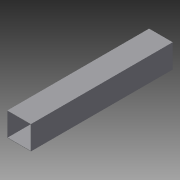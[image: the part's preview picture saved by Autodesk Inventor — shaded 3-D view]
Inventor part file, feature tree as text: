
AUTODESK INVENTOR PART (.ipt)
format: ipt  version: 2015 SP1 (Build 190203100, 203)  size: 75,264 bytes
history: native  units: in
note: dims shown in document units (in); Inventor stores cm internally (conversion verified against a paired STEP export)
features: extrude x1, sketch x1
ambient origin geometry x8: Origin, YZ Plane, XZ Plane, XY Plane, X Axis, Y Axis, Z Axis, Center Point
bodies: Solid1 (feature_tree)
feature tree (2):
  extrude  "Extrusion1"  Depth=2.0in
  sketch  "Sketch1"  dims[d0=2.0in d1=2.0in d2=0.03in d3=12.0in d4=0.0in]
